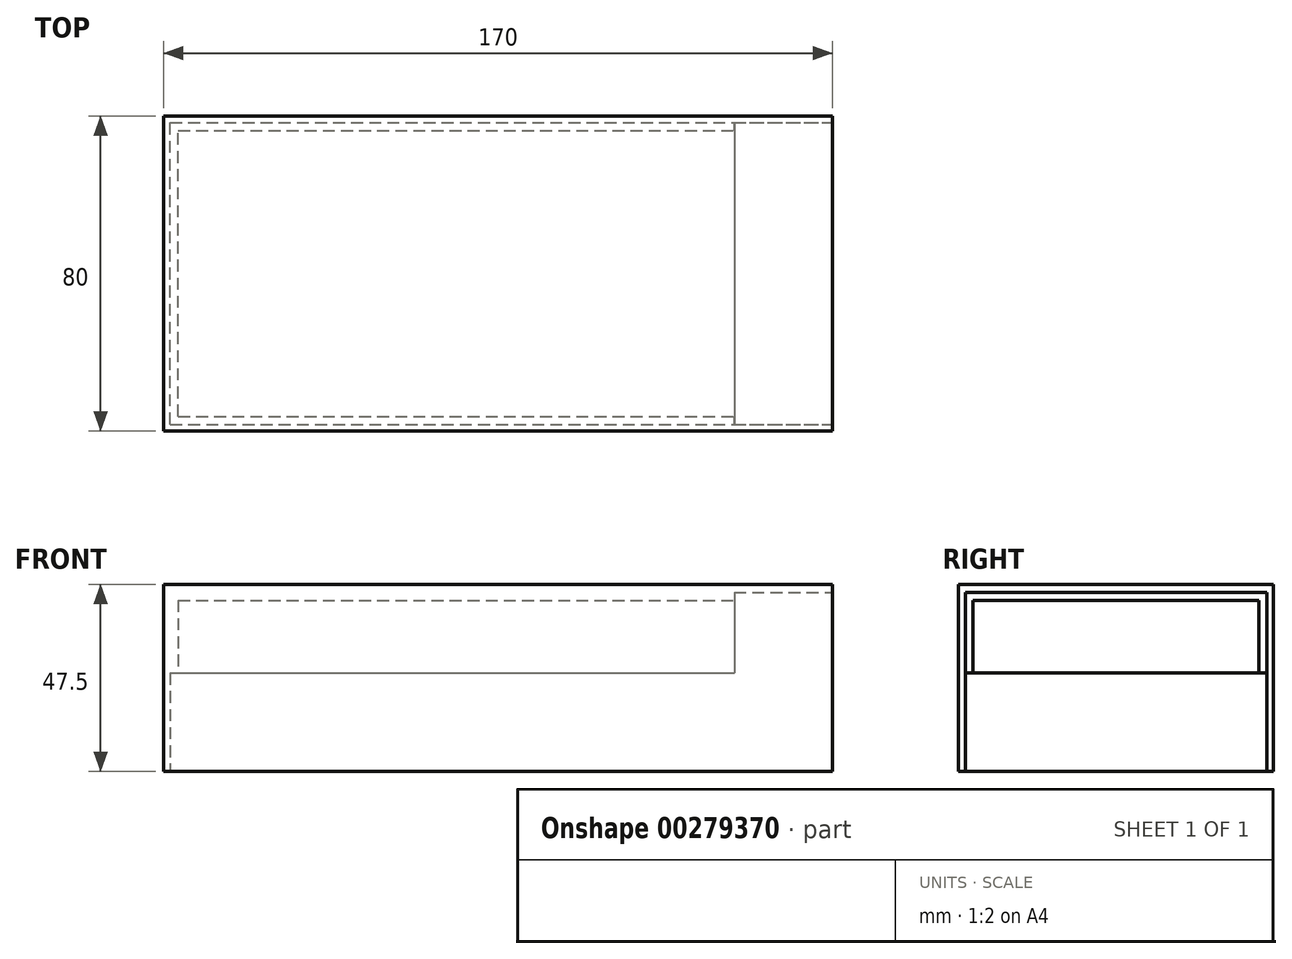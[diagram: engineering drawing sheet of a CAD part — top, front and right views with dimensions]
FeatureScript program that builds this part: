
annotation { "Feature Type Name" : "Feature", "Feature Type Description" : "" }
export const myFeature = defineFeature(function(context is Context, id is Id, definition is map)
    precondition{}
    {
        {
            var Q0;
            Q0=qCreatedBy(makeId("Top.planeOp"),FACE);
            var sketch = newSketch(context, id + "F0", { "sketchPlane" : qUnion([Q0])});
            skLineSegment(sketch, "E0", {"start": v(-189.63, 0) * mm, "end": v(207.94, 0) * mm, "construction": true});
            skLineSegment(sketch, "E1", {"start": v(0, 67.33) * mm, "end": v(0, -76.99) * mm, "construction": true});
            skLineSegment(sketch, "E2.0", {"start": v(-166, 36) * mm, "end": v(0, 36) * mm});
            skLineSegment(sketch, "E3.0", {"start": v(-166, 36) * mm, "end": v(-166, 0) * mm});
            skLineSegment(sketch, "E4.MirrorCS", {"start": v(-166, -36) * mm, "end": v(-166, 0) * mm});
            skLineSegment(sketch, "E5.MirrorCS", {"start": v(-166, -36) * mm, "end": v(0, -36) * mm});
            skLineSegment(sketch, "E6.0", {"start": v(-170, 40) * mm, "end": v(0, 40) * mm});
            skLineSegment(sketch, "E7.0", {"start": v(-170, 40) * mm, "end": v(-170, -40) * mm});
            skLineSegment(sketch, "E8.0", {"start": v(-170, -40) * mm, "end": v(0, -40) * mm});
            skLineSegment(sketch, "E9", {"start": v(0, 40) * mm, "end": v(0, 36) * mm});
            skLineSegment(sketch, "E10", {"start": v(0, -36) * mm, "end": v(0, -40) * mm});
            skLineSegment(sketch, "E11", {"start": v(0, 36) * mm, "end": v(0, -36) * mm});
            skSolve(sketch);
        }
        {
            var Q0;
            Q0=makeQuery(id+"F0.imprint","IMPRINT",FACE,{"disambiguationData":[TD([[makeQuery(id+"F0.imprint","IMPRINT",EDGE,{"derivedFrom":sQuery(id+"F0.wireOp",EDGE,"E2.0")}),1.0]])]});
            extrude(context, id + "F1", {"entities" : qUnion([Q0]), "depth" : 43.5 * mm, "offsetDistance" : 25 * mm});
        }
        {
            var Q0;
            Q0=makeQuery(id+"F1.opExtrude","CAP_FACE",FACE,{"disambiguationData":[OSD([sQuery(id+"F0.wireOp",EDGE,"E2.0"),sQuery(id+"F0.wireOp",EDGE,"E3.0"),sQuery(id+"F0.wireOp",EDGE,"E4.MirrorCS"),sQuery(id+"F0.wireOp",EDGE,"E5.MirrorCS"),sQuery(id+"F0.wireOp",EDGE,"E6.0"),sQuery(id+"F0.wireOp",EDGE,"E7.0"),sQuery(id+"F0.wireOp",EDGE,"E8.0"),sQuery(id+"F0.wireOp",EDGE,"E9"),sQuery(id+"F0.wireOp",EDGE,"E10")])],"isStart":false});
            var sketch = newSketch(context, id + "F2", { "sketchPlane" : qUnion([Q0])});
            skLineSegment(sketch, "E12.0", {"start": v(-170, 40) * mm, "end": v(0, 40) * mm});
            skLineSegment(sketch, "E13.0", {"start": v(-170, 40) * mm, "end": v(-170, -40) * mm});
            skLineSegment(sketch, "E14.0", {"start": v(-170, -40) * mm, "end": v(0, -40) * mm});
            skLineSegment(sketch, "E15", {"start": v(0, 40) * mm, "end": v(0, -40) * mm});
            skSolve(sketch);
        }
        {
            var Q0;
            Q0 = qSketchRegion(id + "F2", true);
            extrude(context, id + "F3", {"entities" : qUnion([Q0]), "operationType" : NewBodyOperationType.ADD, "depth" : 4 * mm, "offsetDistance" : 25 * mm});
        }
        {
            var Q0;
            Q0=makeQuery(id+"F0.imprint","IMPRINT",FACE,{"disambiguationData":[TD([[makeQuery(id+"F0.imprint","IMPRINT",EDGE,{"derivedFrom":sQuery(id+"F0.wireOp",EDGE,"E2.0")}),1.0]])]});
            var sketch = newSketch(context, id + "F4", { "sketchPlane" : qUnion([Q0])});
            skLineSegment(sketch, "E16.0", {"start": v(-166, -36) * mm, "end": v(0, -36) * mm});
            skLineSegment(sketch, "E17.0", {"start": v(-166, -36) * mm, "end": v(-166, 36) * mm});
            skLineSegment(sketch, "E18.0", {"start": v(-166, 36) * mm, "end": v(0, 36) * mm});
            skLineSegment(sketch, "E19.0", {"start": v(-168, -38) * mm, "end": v(0, -38) * mm});
            skLineSegment(sketch, "E20.0", {"start": v(-168, 38) * mm, "end": v(0, 38) * mm});
            skLineSegment(sketch, "E21.0", {"start": v(-168, -38) * mm, "end": v(-168, 38) * mm});
            skPoint(sketch, "E22.orphan", {"position": v(-166, 0) * mm});
            skLineSegment(sketch, "E23.0", {"start": v(0, -36) * mm, "end": v(0, -38) * mm});
            skLineSegment(sketch, "E24.0", {"start": v(0, 38) * mm, "end": v(0, 36) * mm});
            skPoint(sketch, "E25.orphan", {"position": v(0, 36) * mm});
            skPoint(sketch, "E26.orphan", {"position": v(0, 40) * mm});
            skPoint(sketch, "E27.orphan", {"position": v(0, -40) * mm});
            skSolve(sketch);
        }
        {
            var Q0;
            {var subQ3=sQuery(id+"F4.wireOp",EDGE,"E16.0");Q0=makeQuery(id+"F4.imprint","IMPRINT",FACE,{"disambiguationData":[TD([[makeQuery(id+"F4.imprint","IMPRINT",EDGE,{"derivedFrom":subQ3}),-1.0]])]});}
            extrude(context, id + "F5", {"entities" : qUnion([Q0]), "operationType" : NewBodyOperationType.REMOVE, "depth" : 25 * mm, "offsetDistance" : 25 * mm});
        }
        {
            var Q0;
            Q0=makeQuery(id+"F0.imprint","IMPRINT",FACE,{"disambiguationData":[TD([[makeQuery(id+"F0.imprint","IMPRINT",EDGE,{"derivedFrom":sQuery(id+"F0.wireOp",EDGE,"E2.0")}),1.0]])]});
            var sketch = newSketch(context, id + "F6", { "sketchPlane" : qUnion([Q0])});
            skLineSegment(sketch, "E28.0", {"start": v(0, 38) * mm, "end": v(0, -38) * mm});
            skLineSegment(sketch, "E29.0", {"start": v(-25, -38) * mm, "end": v(0, -38) * mm});
            skLineSegment(sketch, "E30.0", {"start": v(-25, 38) * mm, "end": v(-25, -38) * mm});
            skPoint(sketch, "E31.orphan", {"position": v(0, -76.99) * mm});
            skPoint(sketch, "E32.orphan", {"position": v(-168, -38) * mm});
            skLineSegment(sketch, "E33.0", {"start": v(-25, 38) * mm, "end": v(0, 38) * mm});
            skPoint(sketch, "E34.orphan", {"position": v(-168, 38) * mm});
            skPoint(sketch, "E35.orphan", {"position": v(0, 67.33) * mm});
            skSolve(sketch);
        }
        {
            var Q0;
            {var subQ3=sQuery(id+"F6.wireOp",EDGE,"E29.0");Q0=makeQuery(id+"F6.imprint","IMPRINT",FACE,{"disambiguationData":[TD([[makeQuery(id+"F6.imprint","IMPRINT",EDGE,{"derivedFrom":subQ3}),1.0]])]});}
            var Q1;
            {var subQ0=sQuery(id+"F6.wireOp",EDGE,"E28.0");var subQ1=makeQuery(id+"F0.imprint","IMPRINT",EDGE,{"derivedFrom":sQuery(id+"F0.wireOp",EDGE,"E2.0")});var subQ2=makeQuery(id+"F6.imprint","INTERSECT",VERTEX,{"derivedFrom":[subQ1,subQ0]});Q1=makeQuery(id+"F6.imprint","IMPRINT",FACE,{"disambiguationData":[TD([[makeQuery(id+"F6.imprint","IMPRINT",EDGE,{"disambiguationData":[TD([[subQ2,-1.0]])],"derivedFrom":subQ0}),-1.0]])]});}
            var Q2;
            {var subQ3=sQuery(id+"F6.wireOp",EDGE,"E33.0");Q2=makeQuery(id+"F6.imprint","IMPRINT",FACE,{"disambiguationData":[TD([[makeQuery(id+"F6.imprint","IMPRINT",EDGE,{"derivedFrom":subQ3}),-1.0]])]});}
            extrude(context, id + "F7", {"entities" : qUnion([Q0, Q1, Q2]), "operationType" : NewBodyOperationType.REMOVE, "depth" : 43.5 * mm, "offsetDistance" : 25 * mm});
        }
        {
            var Q0;
            Q0=makeQuery(id+"F1.opExtrude","CAP_FACE",FACE,{"disambiguationData":[OSD([sQuery(id+"F0.wireOp",EDGE,"E2.0"),sQuery(id+"F0.wireOp",EDGE,"E3.0"),sQuery(id+"F0.wireOp",EDGE,"E4.MirrorCS"),sQuery(id+"F0.wireOp",EDGE,"E5.MirrorCS"),sQuery(id+"F0.wireOp",EDGE,"E6.0"),sQuery(id+"F0.wireOp",EDGE,"E7.0"),sQuery(id+"F0.wireOp",EDGE,"E8.0"),sQuery(id+"F0.wireOp",EDGE,"E9"),sQuery(id+"F0.wireOp",EDGE,"E10")])],"isStart":true});
            var sketch = newSketch(context, id + "F8", { "sketchPlane" : qUnion([Q0])});
            skLineSegment(sketch, "E36.0", {"start": v(-168, 38) * mm, "end": v(0, 38) * mm});
            skLineSegment(sketch, "E37.0", {"start": v(-168, 38) * mm, "end": v(-168, -38) * mm});
            skLineSegment(sketch, "E38.0", {"start": v(-168, -38) * mm, "end": v(0, -38) * mm});
            skLineSegment(sketch, "E39.0", {"start": v(0, 38) * mm, "end": v(0, 38.3) * mm});
            skLineSegment(sketch, "E40.0", {"start": v(0, -38.3) * mm, "end": v(0, -38) * mm});
            skLineSegment(sketch, "E41.0", {"start": v(-168.3, 38.3) * mm, "end": v(0, 38.3) * mm});
            skLineSegment(sketch, "E42.0", {"start": v(-168.3, 38.3) * mm, "end": v(-168.3, -38.3) * mm});
            skLineSegment(sketch, "E43.0", {"start": v(-168.3, -38.3) * mm, "end": v(0, -38.3) * mm});
            skPoint(sketch, "E44.orphan", {"position": v(0, -40) * mm});
            skPoint(sketch, "E45.orphan", {"position": v(0, 40) * mm});
            skSolve(sketch);
        }
        {
            var Q0;
            Q0=makeQuery(id+"F8.imprint","IMPRINT",FACE,{"disambiguationData":[TD([[makeQuery(id+"F8.imprint","IMPRINT",EDGE,{"derivedFrom":sQuery(id+"F8.wireOp",EDGE,"E36.0")}),1.0]])]});
            extrude(context, id + "F9", {"entities" : qUnion([Q0]), "operationType" : NewBodyOperationType.REMOVE, "oppositeDirection" : true, "depth" : 25 * mm, "offsetDistance" : 25 * mm});
        }
        {
            var Q0;
            Q0=makeQuery(id+"F9.boolean.opBoolean","MERGE",FACE,{"derivedFrom":[makeQuery(id+"F5.boolean.opBoolean","COPY",FACE,{"derivedFrom":makeQuery(id+"F5.opExtrude","CAP_FACE",FACE,{"disambiguationData":[OSD([sQuery(id+"F4.wireOp",EDGE,"E16.0"),sQuery(id+"F4.wireOp",EDGE,"E17.0"),sQuery(id+"F4.wireOp",EDGE,"E18.0"),sQuery(id+"F4.wireOp",EDGE,"E19.0"),sQuery(id+"F4.wireOp",EDGE,"E20.0"),sQuery(id+"F4.wireOp",EDGE,"E21.0"),sQuery(id+"F4.wireOp",EDGE,"E23.0"),sQuery(id+"F4.wireOp",EDGE,"E24.0")])],"isStart":false})}),makeQuery(id+"F9.opExtrude","CAP_FACE",FACE,{"disambiguationData":[OSD([sQuery(id+"F8.wireOp",EDGE,"E36.0"),sQuery(id+"F8.wireOp",EDGE,"E37.0"),sQuery(id+"F8.wireOp",EDGE,"E38.0"),sQuery(id+"F8.wireOp",EDGE,"E39.0"),sQuery(id+"F8.wireOp",EDGE,"E40.0"),sQuery(id+"F8.wireOp",EDGE,"E41.0"),sQuery(id+"F8.wireOp",EDGE,"E42.0"),sQuery(id+"F8.wireOp",EDGE,"E43.0")])],"isStart":false})]});
            var sketch = newSketch(context, id + "F10", { "sketchPlane" : qUnion([Q0])});
            skLineSegment(sketch, "E46.0", {"start": v(-25, 38) * mm, "end": v(0, 38) * mm});
            skLineSegment(sketch, "E47.0", {"start": v(-168.3, 38.3) * mm, "end": v(0, 38.3) * mm});
            skLineSegment(sketch, "E48.0", {"start": v(-25, 38.3) * mm, "end": v(-25, 38) * mm});
            skPoint(sketch, "E49.orphan", {"position": v(-25, 36) * mm});
            skLineSegment(sketch, "E50", {"start": v(0, 38.3) * mm, "end": v(0, 38) * mm});
            skSolve(sketch);
        }
        {
            var Q0;
            Q0 = qSketchRegion(id + "F10", true);
            extrude(context, id + "F11", {"entities" : qUnion([Q0]), "operationType" : NewBodyOperationType.REMOVE, "oppositeDirection" : true, "depth" : (43.5 - 25) * mm, "offsetDistance" : 25 * mm});
        }
        {
            var Q0;
            Q0=makeQuery(id+"F9.boolean.opBoolean","MERGE",FACE,{"derivedFrom":[makeQuery(id+"F5.boolean.opBoolean","COPY",FACE,{"derivedFrom":makeQuery(id+"F5.opExtrude","CAP_FACE",FACE,{"disambiguationData":[OSD([sQuery(id+"F4.wireOp",EDGE,"E16.0"),sQuery(id+"F4.wireOp",EDGE,"E17.0"),sQuery(id+"F4.wireOp",EDGE,"E18.0"),sQuery(id+"F4.wireOp",EDGE,"E19.0"),sQuery(id+"F4.wireOp",EDGE,"E20.0"),sQuery(id+"F4.wireOp",EDGE,"E21.0"),sQuery(id+"F4.wireOp",EDGE,"E23.0"),sQuery(id+"F4.wireOp",EDGE,"E24.0")])],"isStart":false})}),makeQuery(id+"F9.opExtrude","CAP_FACE",FACE,{"disambiguationData":[OSD([sQuery(id+"F8.wireOp",EDGE,"E36.0"),sQuery(id+"F8.wireOp",EDGE,"E37.0"),sQuery(id+"F8.wireOp",EDGE,"E38.0"),sQuery(id+"F8.wireOp",EDGE,"E39.0"),sQuery(id+"F8.wireOp",EDGE,"E40.0"),sQuery(id+"F8.wireOp",EDGE,"E41.0"),sQuery(id+"F8.wireOp",EDGE,"E42.0"),sQuery(id+"F8.wireOp",EDGE,"E43.0")])],"isStart":false})]});
            var sketch = newSketch(context, id + "F12", { "sketchPlane" : qUnion([Q0])});
            skLineSegment(sketch, "E51.0", {"start": v(-166, 36) * mm, "end": v(-25, 36) * mm});
            skLineSegment(sketch, "E52.0", {"start": v(-166, 36) * mm, "end": v(-166, -36) * mm});
            skLineSegment(sketch, "E53.0", {"start": v(-25, 36.3) * mm, "end": v(-25, 36) * mm});
            skLineSegment(sketch, "E54.0", {"start": v(-25, -36) * mm, "end": v(-25, -36.3) * mm});
            skLineSegment(sketch, "E55.0", {"start": v(-166, -36) * mm, "end": v(-25, -36) * mm});
            skLineSegment(sketch, "E56.0", {"start": v(-166.3, 36.3) * mm, "end": v(-25, 36.3) * mm});
            skLineSegment(sketch, "E57.0", {"start": v(-166.3, 36.3) * mm, "end": v(-166.3, -36.3) * mm});
            skLineSegment(sketch, "E58.0", {"start": v(-166.3, -36.3) * mm, "end": v(-25, -36.3) * mm});
            skPoint(sketch, "E59.orphan", {"position": v(-25, -38) * mm});
            skPoint(sketch, "E60.orphan", {"position": v(-25, 38.3) * mm});
            skSolve(sketch);
        }
        {
            var Q0;
            Q0 = qSketchRegion(id + "F12", true);
            extrude(context, id + "F13", {"entities" : qUnion([Q0]), "operationType" : NewBodyOperationType.REMOVE, "oppositeDirection" : true, "depth" : (43.5 - 25) * mm, "offsetDistance" : 25 * mm});
        }
        {
            var Q0;
            Q0=makeQuery(id+"F9.boolean.opBoolean","MERGE",FACE,{"derivedFrom":[makeQuery(id+"F5.boolean.opBoolean","COPY",FACE,{"derivedFrom":makeQuery(id+"F5.opExtrude","CAP_FACE",FACE,{"disambiguationData":[OSD([sQuery(id+"F4.wireOp",EDGE,"E16.0"),sQuery(id+"F4.wireOp",EDGE,"E17.0"),sQuery(id+"F4.wireOp",EDGE,"E18.0"),sQuery(id+"F4.wireOp",EDGE,"E19.0"),sQuery(id+"F4.wireOp",EDGE,"E20.0"),sQuery(id+"F4.wireOp",EDGE,"E21.0"),sQuery(id+"F4.wireOp",EDGE,"E23.0"),sQuery(id+"F4.wireOp",EDGE,"E24.0")])],"isStart":false})}),makeQuery(id+"F9.opExtrude","CAP_FACE",FACE,{"disambiguationData":[OSD([sQuery(id+"F8.wireOp",EDGE,"E36.0"),sQuery(id+"F8.wireOp",EDGE,"E37.0"),sQuery(id+"F8.wireOp",EDGE,"E38.0"),sQuery(id+"F8.wireOp",EDGE,"E39.0"),sQuery(id+"F8.wireOp",EDGE,"E40.0"),sQuery(id+"F8.wireOp",EDGE,"E41.0"),sQuery(id+"F8.wireOp",EDGE,"E42.0"),sQuery(id+"F8.wireOp",EDGE,"E43.0")])],"isStart":false})]});
            var sketch = newSketch(context, id + "F14", { "sketchPlane" : qUnion([Q0])});
            skLineSegment(sketch, "E61.0", {"start": v(-25, -38) * mm, "end": v(0, -38) * mm});
            skLineSegment(sketch, "E62.0", {"start": v(0, -38.3) * mm, "end": v(0, -38) * mm});
            skLineSegment(sketch, "E63.0", {"start": v(-25, -38.3) * mm, "end": v(0, -38.3) * mm});
            skLineSegment(sketch, "E64.0", {"start": v(-25, -38) * mm, "end": v(-25, -38.3) * mm});
            skPoint(sketch, "E65.orphan", {"position": v(-25, -36.3) * mm});
            skPoint(sketch, "E66.orphan", {"position": v(-168.3, -38.3) * mm});
            skSolve(sketch);
        }
        {
            var Q0;
            Q0 = qSketchRegion(id + "F14", true);
            extrude(context, id + "F15", {"entities" : qUnion([Q0]), "operationType" : NewBodyOperationType.REMOVE, "oppositeDirection" : true, "depth" : (43.5 - 25) * mm, "offsetDistance" : 25 * mm});
        }
        {
            var Q0;
            Q0=makeQuery(id+"F3.boolean.opBoolean","MERGE",FACE,{"derivedFrom":[makeQuery(id+"F1.opExtrude","SWEPT_FACE",FACE,{"disambiguationData":[OSD([sQuery(id+"F0.wireOp",EDGE,"E9")])]}),makeQuery(id+"F1.opExtrude","SWEPT_FACE",FACE,{"disambiguationData":[OSD([sQuery(id+"F0.wireOp",EDGE,"E10")])]}),makeQuery(id+"F3.opExtrude","SWEPT_FACE",FACE,{"disambiguationData":[OSD([sQuery(id+"F2.wireOp",EDGE,"E15")])]})]});
            var sketch = newSketch(context, id + "F16", { "sketchPlane" : qUnion([Q0])});
            skLineSegment(sketch, "E67.0", {"start": v(38.3, 43.5) * mm, "end": v(-38.3, 43.5) * mm});
            skLineSegment(sketch, "E68.0", {"start": v(38.3, 45.5) * mm, "end": v(-38.3, 45.5) * mm});
            skLineSegment(sketch, "E69", {"start": v(-38.3, 43.5) * mm, "end": v(-38.3, 45.5) * mm});
            skLineSegment(sketch, "E70", {"start": v(38.3, 43.5) * mm, "end": v(38.3, 45.5) * mm});
            skPoint(sketch, "E71.0.end.orphan", {"position": v(-40, 47.5) * mm});
            skPoint(sketch, "E71.0.start.orphan", {"position": v(40, 47.5) * mm});
            skLineSegment(sketch, "E72", {"start": v(-38.3, 43.5) * mm, "end": v(38.3, 43.5) * mm});
            skSolve(sketch);
        }
        {
            var Q0;
            Q0 = qSketchRegion(id + "F16", true);
            extrude(context, id + "F17", {"entities" : qUnion([Q0]), "operationType" : NewBodyOperationType.REMOVE, "oppositeDirection" : true, "depth" : 25 * mm, "offsetDistance" : 25 * mm});
        }
    });
